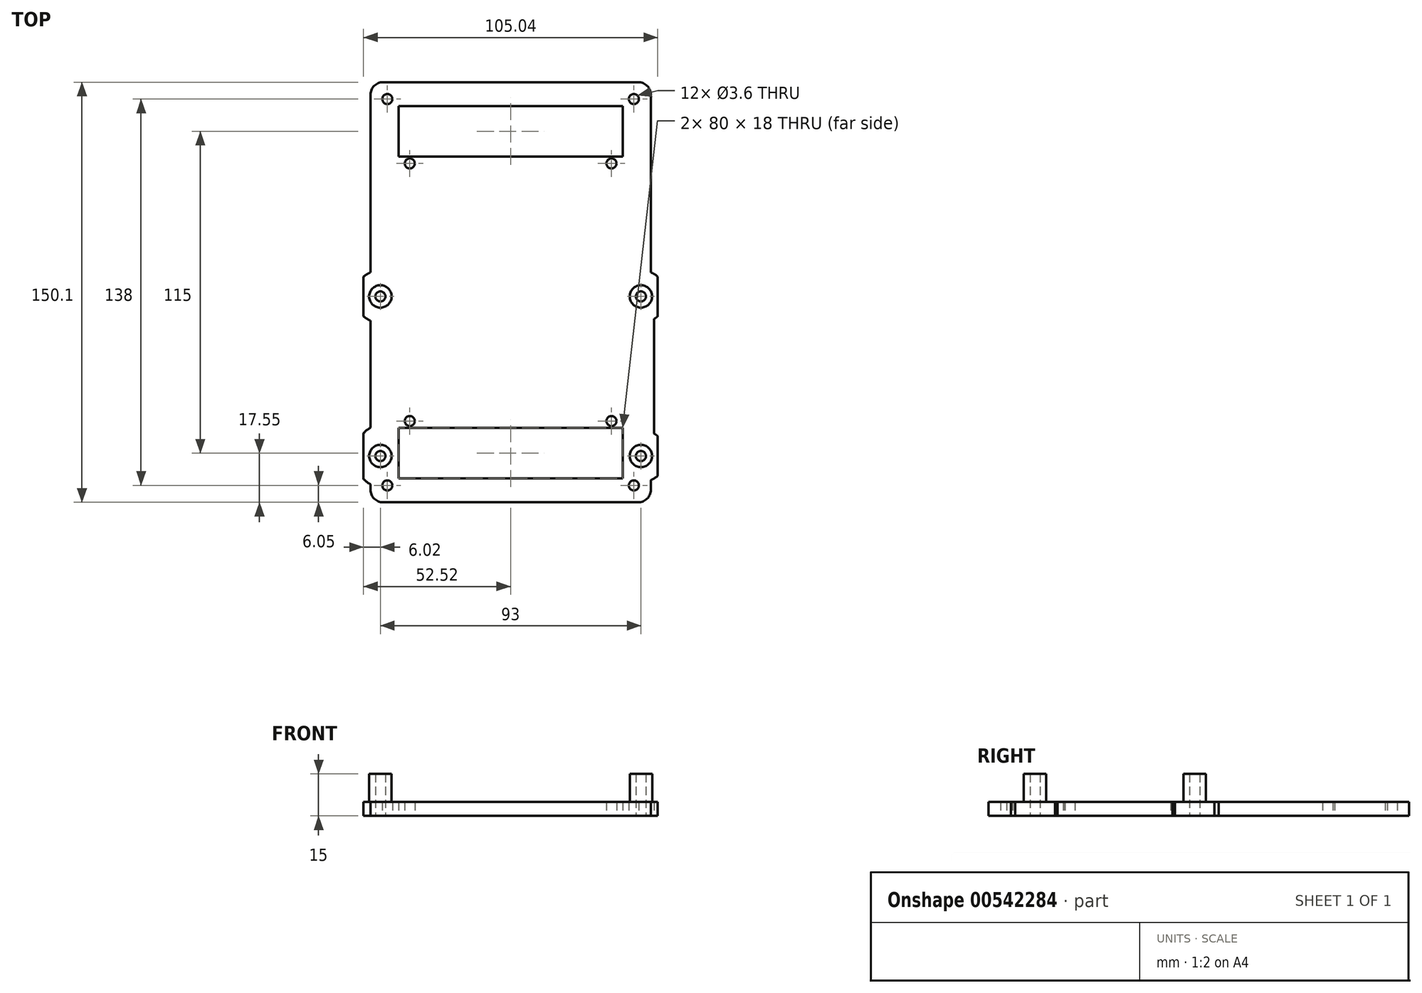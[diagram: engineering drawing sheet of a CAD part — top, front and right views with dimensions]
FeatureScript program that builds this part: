
annotation { "Feature Type Name" : "Feature", "Feature Type Description" : "" }
export const myFeature = defineFeature(function(context is Context, id is Id, definition is map)
    precondition{}
    {
        {
            var Q0;
            Q0=qCreatedBy(makeId("Top.planeOp"),FACE);
            var sketch = newSketch(context, id + "F0", { "sketchPlane" : qUnion([Q0])});
            skLineSegment(sketch, "E0.bottom", {"start": v(-44, 69) * mm, "end": v(44, 69) * mm, "construction": true});
            skLineSegment(sketch, "E0.top", {"start": v(-44, -69) * mm, "end": v(44, -69) * mm, "construction": true});
            skLineSegment(sketch, "E0.left", {"start": v(-44, 69) * mm, "end": v(-44, -69) * mm, "construction": true});
            skLineSegment(sketch, "E0.right", {"start": v(44, 69) * mm, "end": v(44, -69) * mm, "construction": true});
            skPoint(sketch, "E0.middle", {"position": v(0, 0) * mm});
            skLineSegment(sketch, "E1", {"start": v(0, 0) * mm, "end": v(0, -30) * mm, "construction": true});
            skLineSegment(sketch, "E2.bottom", {"start": v(-46.5, -1.5) * mm, "end": v(46.5, -1.5) * mm, "construction": true});
            skLineSegment(sketch, "E2.top", {"start": v(-46.5, -58.5) * mm, "end": v(46.5, -58.5) * mm, "construction": true});
            skLineSegment(sketch, "E2.left", {"start": v(-46.5, -1.5) * mm, "end": v(-46.5, -58.5) * mm, "construction": true});
            skLineSegment(sketch, "E2.right", {"start": v(46.5, -1.5) * mm, "end": v(46.5, -58.5) * mm, "construction": true});
            skPoint(sketch, "E2.middle", {"position": v(0, -30) * mm});
            skLineSegment(sketch, "E3.bottom", {"start": v(-36, 46) * mm, "end": v(36, 46) * mm, "construction": true});
            skLineSegment(sketch, "E3.top", {"start": v(-36, -46) * mm, "end": v(36, -46) * mm, "construction": true});
            skLineSegment(sketch, "E3.left", {"start": v(-36, 46) * mm, "end": v(-36, -46) * mm, "construction": true});
            skLineSegment(sketch, "E3.right", {"start": v(36, 46) * mm, "end": v(36, -46) * mm, "construction": true});
            skLineSegment(sketch, "E4", {"start": v(0, 0) * mm, "end": v(18.66, 0) * mm, "construction": true});
            skCircle(sketch, "E5", {"center": v(-36, 46) * mm, "radius": 1.8 * mm});
            skCircle(sketch, "E6", {"center": v(-44, 69) * mm, "radius": 1.8 * mm});
            skCircle(sketch, "E7", {"center": v(-46.5, -1.5) * mm, "radius": 1.8 * mm});
            skCircle(sketch, "E8.MirrorC", {"center": v(46.5, -1.5) * mm, "radius": 1.8 * mm});
            skCircle(sketch, "E9.MirrorC", {"center": v(36, 46) * mm, "radius": 1.8 * mm});
            skCircle(sketch, "E10.MirrorC", {"center": v(44, 69) * mm, "radius": 1.8 * mm});
            skCircle(sketch, "E11.MirrorC", {"center": v(-36, -46) * mm, "radius": 1.8 * mm});
            skCircle(sketch, "E12.MirrorC", {"center": v(36, -46) * mm, "radius": 1.8 * mm});
            skCircle(sketch, "E13.MirrorC", {"center": v(-44, -69) * mm, "radius": 1.8 * mm});
            skCircle(sketch, "E14.MirrorC", {"center": v(44, -69) * mm, "radius": 1.8 * mm});
            skLineSegment(sketch, "E15", {"start": v(0, -30) * mm, "end": v(15.96, -30) * mm, "construction": true});
            skCircle(sketch, "E16.MirrorC", {"center": v(-46.5, -58.5) * mm, "radius": 1.8 * mm});
            skCircle(sketch, "E17.MirrorC", {"center": v(46.5, -58.5) * mm, "radius": 1.8 * mm});
            skLineSegment(sketch, "E18", {"start": v(-44, 69) * mm, "end": v(-47.52, 72.55) * mm, "construction": true});
            skLineSegment(sketch, "E19", {"start": v(44, -69) * mm, "end": v(47.52, -72.55) * mm, "construction": true});
            skPoint(sketch, "E20.visualSharp", {"position": v(-47.52, 72.55) * mm});
            skPoint(sketch, "E21.visualSharp", {"position": v(47.52, 72.55) * mm});
            skPoint(sketch, "E22.visualSharp", {"position": v(-47.52, -72.55) * mm});
            skPoint(sketch, "E23.visualSharp", {"position": v(47.52, -72.55) * mm});
            skLineSegment(sketch, "E24", {"start": v(0, 46) * mm, "end": v(0, 69) * mm, "construction": true});
            skLineSegment(sketch, "E25.bottom", {"start": v(-40, 66.5) * mm, "end": v(40, 66.5) * mm});
            skLineSegment(sketch, "E25.top", {"start": v(-40, 48.5) * mm, "end": v(40, 48.5) * mm});
            skLineSegment(sketch, "E25.left", {"start": v(-40, 66.5) * mm, "end": v(-40, 48.5) * mm});
            skLineSegment(sketch, "E25.right", {"start": v(40, 66.5) * mm, "end": v(40, 48.5) * mm});
            skPoint(sketch, "E25.middle", {"position": v(0, 57.5) * mm});
            skLineSegment(sketch, "E26.MirrorCS", {"start": v(-40, -66.5) * mm, "end": v(40, -66.5) * mm});
            skLineSegment(sketch, "E27.MirrorCS", {"start": v(-40, -66.5) * mm, "end": v(-40, -48.5) * mm});
            skLineSegment(sketch, "E28.MirrorCS", {"start": v(-40, -48.5) * mm, "end": v(40, -48.5) * mm});
            skLineSegment(sketch, "E29.MirrorCS", {"start": v(40, -66.5) * mm, "end": v(40, -48.5) * mm});
            skArc(sketch, "E30.0", {"start": v(-50.02, -70.55) * mm, "mid": v(-48.7, -73.73) * mm, "end": v(-45.52, -75.05) * mm});
            skLineSegment(sketch, "E30.1", {"start": v(-50.02, -68.65) * mm, "end": v(-50.02, -70.55) * mm});
            skArc(sketch, "E30.2", {"start": v(-50.02, -68.65) * mm, "mid": v(-51.34, -67.74) * mm, "end": v(-52.52, -66.66) * mm});
            skLineSegment(sketch, "E30.3", {"start": v(-50.02, -10.1) * mm, "end": v(-50.02, -48.35) * mm});
            skArc(sketch, "E30.4", {"start": v(-50.02, 7.1) * mm, "mid": v(-51.33, 6.45) * mm, "end": v(-52.52, 5.59) * mm});
            skLineSegment(sketch, "E30.5", {"start": v(51.25, -9.5) * mm, "end": v(51.25, -50.5) * mm});
            skArc(sketch, "E30.6", {"start": v(50.02, -67.1) * mm, "mid": v(51.33, -66.45) * mm, "end": v(52.52, -65.59) * mm});
            skLineSegment(sketch, "E30.7", {"start": v(50.02, -67.1) * mm, "end": v(50.02, -70.55) * mm});
            skArc(sketch, "E30.8", {"start": v(45.52, -75.05) * mm, "mid": v(48.7, -73.73) * mm, "end": v(50.02, -70.55) * mm});
            skArc(sketch, "E30.9", {"start": v(50.02, 7.1) * mm, "mid": v(51.33, 6.45) * mm, "end": v(52.52, 5.59) * mm});
            skLineSegment(sketch, "E30.10", {"start": v(50.02, 70.55) * mm, "end": v(50.02, 7.1) * mm});
            skArc(sketch, "E30.11", {"start": v(50.02, 70.55) * mm, "mid": v(48.7, 73.73) * mm, "end": v(45.52, 75.05) * mm});
            skLineSegment(sketch, "E30.12", {"start": v(-45.52, 75.05) * mm, "end": v(45.52, 75.05) * mm});
            skArc(sketch, "E30.13", {"start": v(-45.52, 75.05) * mm, "mid": v(-48.7, 73.73) * mm, "end": v(-50.02, 70.55) * mm});
            skLineSegment(sketch, "E30.14", {"start": v(-45.52, -75.05) * mm, "end": v(45.52, -75.05) * mm});
            skLineSegment(sketch, "E30.15", {"start": v(-50.02, 70.55) * mm, "end": v(-50.02, 7.1) * mm});
            skLineSegment(sketch, "E31", {"start": v(-50.02, -68.65) * mm, "end": v(-52.52, -68.65) * mm, "construction": true});
            skLineSegment(sketch, "E32", {"start": v(-52.52, -66.66) * mm, "end": v(-52.52, -50.34) * mm});
            skArc(sketch, "E33.trimOffspring", {"start": v(-52.52, -8.59) * mm, "mid": v(-51.33, -9.45) * mm, "end": v(-50.02, -10.1) * mm});
            skLineSegment(sketch, "E34.trimOffspring", {"start": v(-52.52, -8.59) * mm, "end": v(-52.52, 5.59) * mm});
            skArc(sketch, "E35.trimOffspring", {"start": v(-52.52, -50.34) * mm, "mid": v(-51.34, -49.26) * mm, "end": v(-50.02, -48.35) * mm});
            skLineSegment(sketch, "E36", {"start": v(50.02, -67.1) * mm, "end": v(52.52, -67.1) * mm, "construction": true});
            skLineSegment(sketch, "E37", {"start": v(52.52, -65.59) * mm, "end": v(52.52, -51.41) * mm});
            skLineSegment(sketch, "E38.trimOffspring", {"start": v(52.52, -8.59) * mm, "end": v(52.52, 5.59) * mm});
            skArc(sketch, "E39.trimOffspring", {"start": v(52.52, -8.59) * mm, "mid": v(51.9, -9.07) * mm, "end": v(51.25, -9.5) * mm});
            skArc(sketch, "E40.trimOffspring", {"start": v(52.52, -51.41) * mm, "mid": v(51.9, -50.93) * mm, "end": v(51.25, -50.5) * mm});
            skSolve(sketch);
        }
        {
            var Q0;
            Q0=makeQuery(id+"F0.imprint","IMPRINT",FACE,{"disambiguationData":[TD([[makeQuery(id+"F0.imprint","IMPRINT",EDGE,{"derivedFrom":sQuery(id+"F0.wireOp",EDGE,"E5")}),-1.0]])]});
            extrude(context, id + "F1", {"entities" : qUnion([Q0]), "depth" : 5 * mm, "offsetDistance" : 25 * mm});
        }
        {
            var Q0;
            Q0=makeQuery(id+"F1.opExtrude","CAP_FACE",FACE,{"disambiguationData":[OSD([sQuery(id+"F0.wireOp",EDGE,"E5"),sQuery(id+"F0.wireOp",EDGE,"E6"),sQuery(id+"F0.wireOp",EDGE,"E7"),sQuery(id+"F0.wireOp",EDGE,"E8.MirrorC"),sQuery(id+"F0.wireOp",EDGE,"E9.MirrorC"),sQuery(id+"F0.wireOp",EDGE,"E10.MirrorC"),sQuery(id+"F0.wireOp",EDGE,"E11.MirrorC"),sQuery(id+"F0.wireOp",EDGE,"E12.MirrorC"),sQuery(id+"F0.wireOp",EDGE,"E13.MirrorC"),sQuery(id+"F0.wireOp",EDGE,"E14.MirrorC"),sQuery(id+"F0.wireOp",EDGE,"E16.MirrorC"),sQuery(id+"F0.wireOp",EDGE,"E17.MirrorC"),sQuery(id+"F0.wireOp",EDGE,"NyHKX8gH-we7l-2Of8-X1sF-19fRwSNdVa05.bottom"),sQuery(id+"F0.wireOp",EDGE,"NyHKX8gH-we7l-2Of8-X1sF-19fRwSNdVa05.top"),sQuery(id+"F0.wireOp",EDGE,"NyHKX8gH-we7l-2Of8-X1sF-19fRwSNdVa05.left"),sQuery(id+"F0.wireOp",EDGE,"NyHKX8gH-we7l-2Of8-X1sF-19fRwSNdVa05.right"),sQuery(id+"F0.wireOp",EDGE,"E20.filletArc"),sQuery(id+"F0.wireOp",EDGE,"E21.filletArc"),sQuery(id+"F0.wireOp",EDGE,"E22.filletArc"),sQuery(id+"F0.wireOp",EDGE,"E23.filletArc"),sQuery(id+"F0.wireOp",EDGE,"91ef7b58-bcde-4cb7-abaf-e44b1f90ccf0.0"),sQuery(id+"F0.wireOp",EDGE,"ecfd198c-5271-4874-8160-30425fc620ce.0"),sQuery(id+"F0.wireOp",EDGE,"5c802a37-58bb-485b-9e8b-1295c8434c64.0"),sQuery(id+"F0.wireOp",EDGE,"cd14aeca-d42c-4071-a10d-bc428cbd3450.trimOffspring"),sQuery(id+"F0.wireOp",EDGE,"e5773f19-1534-4150-b7a0-bd999031e6f6.trimOffspring"),sQuery(id+"F0.wireOp",EDGE,"45faed9e-f495-46d7-8067-68fd64e43587.trimOffspring"),sQuery(id+"F0.wireOp",EDGE,"4f299f5e-03f4-46ef-b3e6-2dede421f096.trimOffspring"),sQuery(id+"F0.wireOp",EDGE,"5a853106-4494-4db5-af82-b8a1218f5964.trimOffspring"),sQuery(id+"F0.wireOp",EDGE,"E25.bottom"),sQuery(id+"F0.wireOp",EDGE,"E25.top"),sQuery(id+"F0.wireOp",EDGE,"E25.left"),sQuery(id+"F0.wireOp",EDGE,"E25.right"),sQuery(id+"F0.wireOp",EDGE,"E26.MirrorCS"),sQuery(id+"F0.wireOp",EDGE,"E27.MirrorCS"),sQuery(id+"F0.wireOp",EDGE,"E28.MirrorCS"),sQuery(id+"F0.wireOp",EDGE,"E29.MirrorCS")])],"isStart":false});
            var sketch = newSketch(context, id + "F2", { "sketchPlane" : qUnion([Q0])});
            skCircle(sketch, "E41", {"center": v(-46.5, -1.5) * mm, "radius": 4 * mm});
            skCircle(sketch, "E42", {"center": v(46.5, -1.5) * mm, "radius": 4 * mm});
            skCircle(sketch, "E43", {"center": v(46.5, -58.5) * mm, "radius": 4 * mm});
            skCircle(sketch, "E44", {"center": v(-46.5, -58.5) * mm, "radius": 4 * mm});
            skSolve(sketch);
        }
        {
            var Q0;
            Q0=makeQuery(id+"F2.imprint","IMPRINT",FACE,{"disambiguationData":[TD([[makeQuery(id+"F2.imprint","IMPRINT",EDGE,{"derivedFrom":sQuery(id+"F2.wireOp",EDGE,"E43")}),1.0]])]});
            var Q1;
            Q1=makeQuery(id+"F2.imprint","IMPRINT",FACE,{"disambiguationData":[TD([[makeQuery(id+"F2.imprint","IMPRINT",EDGE,{"derivedFrom":sQuery(id+"F2.wireOp",EDGE,"E44")}),1.0]])]});
            var Q2;
            Q2=makeQuery(id+"F2.imprint","IMPRINT",FACE,{"disambiguationData":[TD([[makeQuery(id+"F2.imprint","IMPRINT",EDGE,{"derivedFrom":sQuery(id+"F2.wireOp",EDGE,"E41")}),1.0]])]});
            var Q3;
            Q3=makeQuery(id+"F2.imprint","IMPRINT",FACE,{"disambiguationData":[TD([[makeQuery(id+"F2.imprint","IMPRINT",EDGE,{"derivedFrom":sQuery(id+"F2.wireOp",EDGE,"E42")}),1.0]])]});
            extrude(context, id + "F3", {"entities" : qUnion([Q0, Q1, Q2, Q3]), "operationType" : NewBodyOperationType.ADD, "depth" : 10 * mm, "offsetDistance" : 25 * mm});
        }
    });
